# Revit family: FACB-BR-8DLL_33150
name_source: partatom
category: Plumbing Fixtures
units: mm (PartAtom-declared; Revit-internal decimal feet)

## family parameters
Always vertical = Yes
Cut with Voids When Loaded = No
OmniClass Number = 23.45.00.00
OmniClass Title = Sanitary, Laundry, and Cleaning Equipment
Part Type = Normal
Room Calculation Point = No
Round Connector Dimension = Use Diameter
Shared = No
Work Plane-Based = No

## types (1)
- FACB-BR-8DLL_33150
    Cold Water Consumption = 0 GPM
    Cold Water Flow = 2 GPM
    Cold Water Maximum Pressure = 200.00 psi
    Cold Water Minimum Pressure = 80.00 psi
    Cold Water Size = 1/2"
    Cold Water Temperature Recommended = 40 °F
    Fixture Height = 4' - 0"
    Hot Water Consumption = 0 GPM
    Hot Water Flow = 2 GPM
    Hot Water Maximum Pressure = 200.00 psi
    Hot Water Minimum Pressure = 80.00 psi
    Hot Water Size = 1/2"
    Hot Water Temperature = 40 °F

## geometry (parser evidence)
native form markers: Sweep x12
no freeform markers — native parametric forms only
